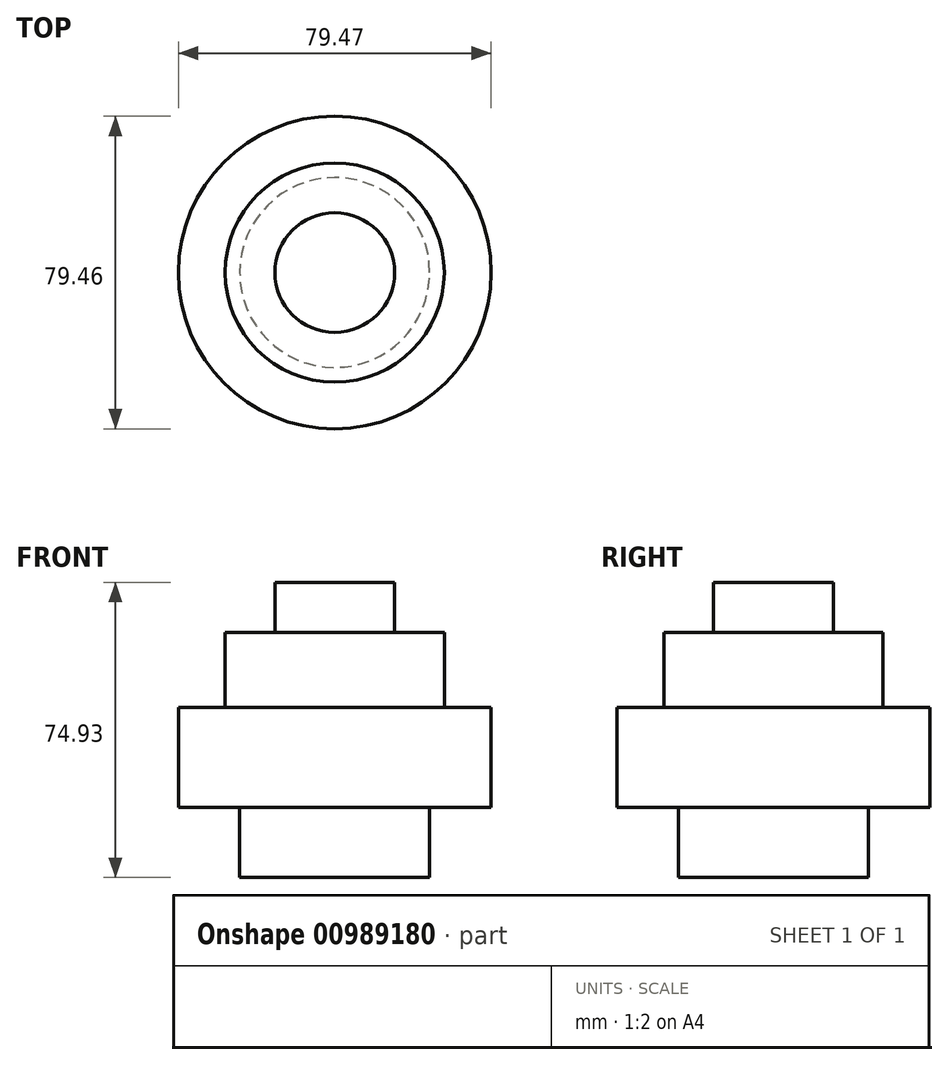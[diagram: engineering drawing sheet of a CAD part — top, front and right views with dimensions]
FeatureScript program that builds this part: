
annotation { "Feature Type Name" : "Feature", "Feature Type Description" : "" }
export const myFeature = defineFeature(function(context is Context, id is Id, definition is map)
    precondition{}
    {
        {
            var Q0;
            Q0=qCreatedBy(makeId("Top.planeOp"),FACE);
            var sketch = newSketch(context, id + "F0", { "sketchPlane" : qUnion([Q0])});
            skCircle(sketch, "E0", {"center": v(-89.23, 10.95) * mm, "radius": 24.13 * mm});
            skSolve(sketch);
        }
        {
            var Q0;
            Q0=makeQuery(id+"F0.imprint","IMPRINT",FACE,{"disambiguationData":[TD([[makeQuery(id+"F0.imprint","IMPRINT",EDGE,{"derivedFrom":sQuery(id+"F0.wireOp",EDGE,"E0")}),1.0]])]});
            extrude(context, id + "F1", {"entities" : qUnion([Q0]), "depth" : 17.78 * mm, "offsetDistance" : 25.4 * mm});
        }
        {
            var Q0;
            Q0=makeQuery(id+"F1.opExtrude","CAP_FACE",FACE,{"disambiguationData":[OSD([sQuery(id+"F0.wireOp",EDGE,"E0")])],"isStart":false});
            var sketch = newSketch(context, id + "F2", { "sketchPlane" : qUnion([Q0])});
            skCircle(sketch, "E1", {"center": v(-89.23, 10.95) * mm, "radius": 39.73 * mm});
            skSolve(sketch);
        }
        {
            var Q0;
            Q0=makeQuery(id+"F2.imprint","IMPRINT",FACE,{"disambiguationData":[TD([[makeQuery(id+"F2.imprint","IMPRINT",EDGE,{"derivedFrom":sQuery(id+"F2.wireOp",EDGE,"E1")}),1.0]])]});
            var Q1;
            Q1=makeQuery(id+"F2.imprint","IMPRINT",FACE,{"disambiguationData":[TD([[makeQuery(id+"F2.imprint","IMPRINT",EDGE,{"derivedFrom":makeQuery(id+"F1.opExtrude","CAP_EDGE",EDGE,{"disambiguationData":[OSD([sQuery(id+"F0.wireOp",EDGE,"E0")])],"isStart":false})}),1.0]])]});
            extrude(context, id + "F3", {"entities" : qUnion([Q0, Q1]), "operationType" : NewBodyOperationType.ADD, "depth" : 25.4 * mm, "offsetDistance" : 25.4 * mm});
        }
        {
            var Q0;
            Q0=makeQuery(id+"F3.opExtrude","CAP_FACE",FACE,{"disambiguationData":[OSD([sQuery(id+"F2.wireOp",EDGE,"E1")])],"isStart":false});
            var sketch = newSketch(context, id + "F4", { "sketchPlane" : qUnion([Q0])});
            skCircle(sketch, "E2", {"center": v(-89.23, 10.95) * mm, "radius": 27.84 * mm});
            skSolve(sketch);
        }
        {
            var Q0;
            Q0=makeQuery(id+"F4.imprint","IMPRINT",FACE,{"disambiguationData":[TD([[makeQuery(id+"F4.imprint","IMPRINT",EDGE,{"derivedFrom":sQuery(id+"F4.wireOp",EDGE,"E2")}),1.0]])]});
            extrude(context, id + "F5", {"entities" : qUnion([Q0]), "operationType" : NewBodyOperationType.ADD, "depth" : 19.05 * mm, "offsetDistance" : 25.4 * mm});
        }
        {
            var Q0;
            Q0=makeQuery(id+"F5.opExtrude","CAP_FACE",FACE,{"disambiguationData":[OSD([sQuery(id+"F4.wireOp",EDGE,"E2")])],"isStart":false});
            var sketch = newSketch(context, id + "F6", { "sketchPlane" : qUnion([Q0])});
            skCircle(sketch, "E3", {"center": v(-89.23, 10.95) * mm, "radius": 15.21 * mm});
            skSolve(sketch);
        }
        {
            var Q0;
            Q0=makeQuery(id+"F6.imprint","IMPRINT",FACE,{"disambiguationData":[TD([[makeQuery(id+"F6.imprint","IMPRINT",EDGE,{"derivedFrom":sQuery(id+"F6.wireOp",EDGE,"E3")}),1.0]])]});
            extrude(context, id + "F7", {"entities" : qUnion([Q0]), "operationType" : NewBodyOperationType.ADD, "depth" : 12.7 * mm, "offsetDistance" : 25.4 * mm});
        }
    });
